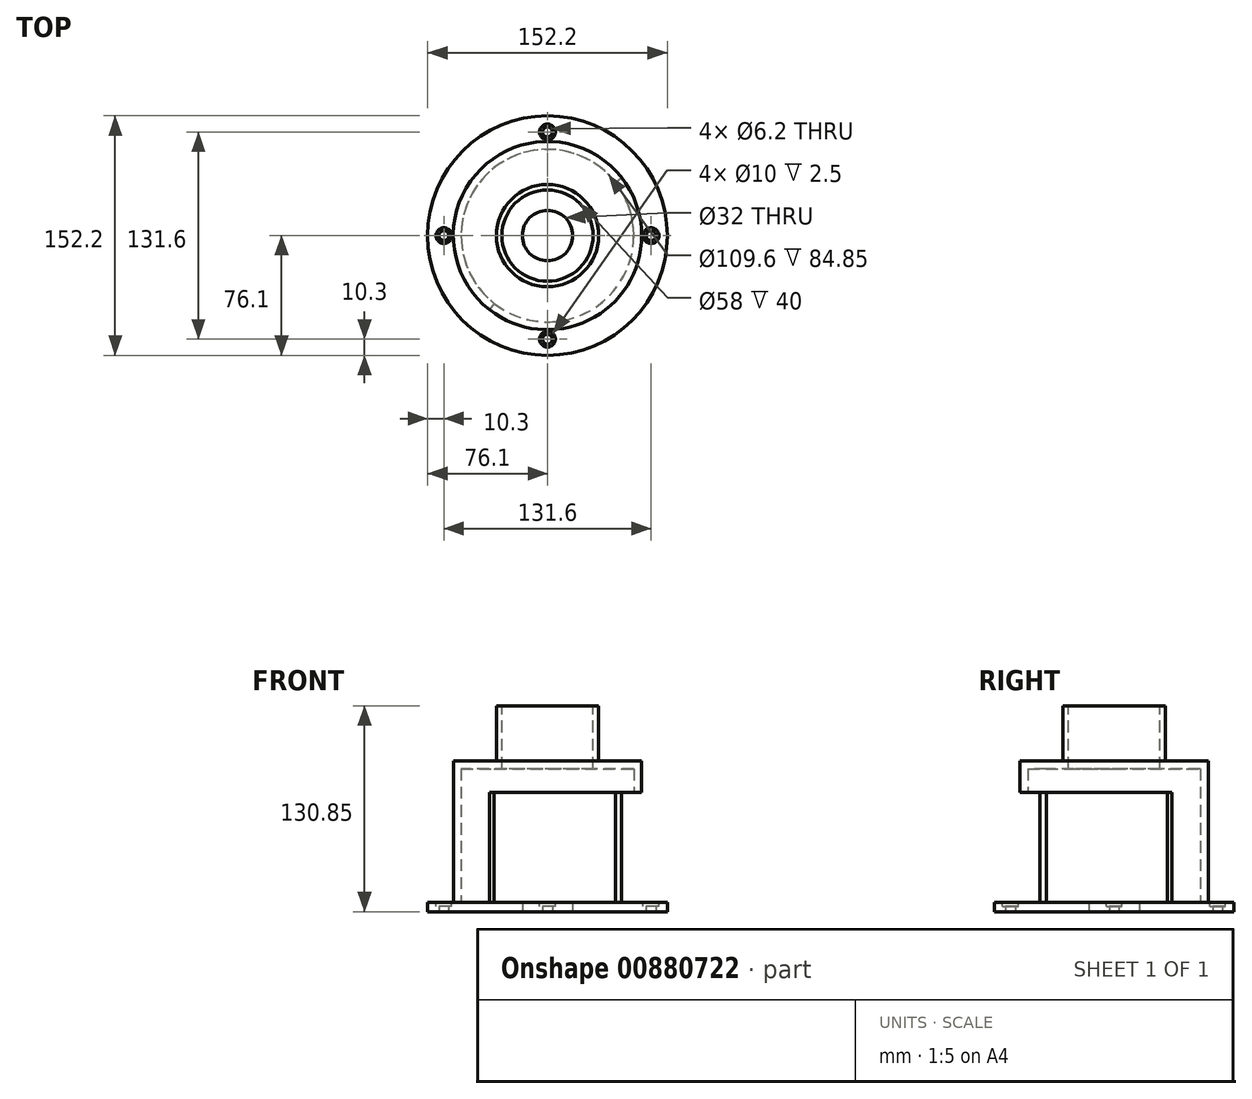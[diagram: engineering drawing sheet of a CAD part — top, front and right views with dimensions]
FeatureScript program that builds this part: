
annotation { "Feature Type Name" : "Feature", "Feature Type Description" : "" }
export const myFeature = defineFeature(function(context is Context, id is Id, definition is map)
    precondition{}
    {
        {
            var Q0;
            Q0=qCreatedBy(makeId("Top.planeOp"),FACE);
            var sketch = newSketch(context, id + "F0", { "sketchPlane" : qUnion([Q0])});
            skCircle(sketch, "E0", {"center": v(0, 0) * mm, "radius": 76.1 * mm});
            skSolve(sketch);
        }
        {
            var Q0;
            Q0 = qSketchRegion(id + "F0", true);
            extrude(context, id + "F1", {"entities" : qUnion([Q0]), "depth" : 6 * mm, "offsetDistance" : 25 * mm});
        }
        {
            var Q0;
            Q0=qCreatedBy(makeId("Top.planeOp"),FACE);
            var sketch = newSketch(context, id + "F2", { "sketchPlane" : qUnion([Q0])});
            skCircle(sketch, "E1", {"center": v(0, 65.8) * mm, "radius": 3.1 * mm});
            skCircle(sketch, "E2", {"center": v(65.8, 0) * mm, "radius": 3.1 * mm});
            skCircle(sketch, "E3", {"center": v(0, -65.8) * mm, "radius": 3.1 * mm});
            skCircle(sketch, "E4", {"center": v(-65.8, 0) * mm, "radius": 3.1 * mm});
            skCircle(sketch, "E5", {"center": v(0, 0) * mm, "radius": 16 * mm});
            skSolve(sketch);
        }
        {
            var Q0;
            Q0 = qSketchRegion(id + "F2", true);
            var Q1;
            Q1=makeQuery(id+"F1.opExtrude","CAP_FACE",FACE,{"disambiguationData":[OSD([sQuery(id+"F0.wireOp",EDGE,"E0")])],"isStart":false});
            extrude(context, id + "F3", {"entities" : qUnion([Q0]), "operationType" : NewBodyOperationType.REMOVE, "endBound" : BoundingType.UP_TO_SURFACE, "depth" : 25 * mm, "endBoundEntityFace" : qUnion([Q1]), "offsetDistance" : 25 * mm});
        }
        {
            var Q0;
            Q0=makeQuery(id+"F1.opExtrude","CAP_FACE",FACE,{"disambiguationData":[OSD([sQuery(id+"F0.wireOp",EDGE,"E0")])],"isStart":false});
            cPlane(context, id + "F4", {"entities" : qUnion([Q0]), "cplaneType" : CPlaneType.OFFSET, "offset" : 0 * mm, "width" : 150 * mm, "height" : 150 * mm});
        }
        {
            var Q0;
            Q0=qCreatedBy(id+"F4.planeOp",FACE);
            var sketch = newSketch(context, id + "F5", { "sketchPlane" : qUnion([Q0])});
            skCircle(sketch, "E6", {"center": v(-0.09, 0) * mm, "radius": 59.89 * mm, "construction": true});
            skCircle(sketch, "E7", {"center": v(0, 0) * mm, "radius": 54.8 * mm, "construction": true});
            skCircle(sketch, "E8.0", {"center": v(65.8, 0) * mm, "radius": 3.1 * mm, "construction": true});
            skLineSegment(sketch, "E9", {"start": v(-0.09, 0) * mm, "end": v(-36.96, -47.2) * mm, "construction": true});
            skLineSegment(sketch, "E10", {"start": v(0, 0) * mm, "end": v(47.14, 36.83) * mm, "construction": true});
            skArc(sketch, "E11", {"start": v(47.14, 36.83) * mm, "mid": v(-42.27, 42.32) * mm, "end": v(-36.88, -47.1) * mm});
            skArc(sketch, "E12", {"start": v(43.18, 33.74) * mm, "mid": v(-38.72, 38.77) * mm, "end": v(-33.8, -43.14) * mm});
            skLineSegment(sketch, "E13", {"start": v(-33.8, -43.14) * mm, "end": v(-36.88, -47.1) * mm});
            skLineSegment(sketch, "E14", {"start": v(43.18, 33.74) * mm, "end": v(47.14, 36.83) * mm});
            skCircle(sketch, "E15", {"center": v(0, 0) * mm, "radius": 12.7 * mm, "construction": true});
            skLineSegment(sketch, "E16", {"start": v(47.14, 36.83) * mm, "end": v(-36.88, -47.1) * mm, "construction": true});
            skSolve(sketch);
        }
        {
            var Q0;
            Q0 = qSketchRegion(id + "F5", true);
            extrude(context, id + "F6", {"entities" : qUnion([Q0]), "operationType" : NewBodyOperationType.ADD, "depth" : 69.85 * mm, "offsetDistance" : 25 * mm});
        }
        {
            var Q0;
            Q0=makeQuery(id+"F6.opExtrude","CAP_FACE",FACE,{"disambiguationData":[OSD([sQuery(id+"F5.wireOp",EDGE,"E11"),sQuery(id+"F5.wireOp",EDGE,"E12"),sQuery(id+"F5.wireOp",EDGE,"E13"),sQuery(id+"F5.wireOp",EDGE,"E14")])],"isStart":false});
            cPlane(context, id + "F7", {"entities" : qUnion([Q0]), "cplaneType" : CPlaneType.OFFSET, "offset" : 0 * mm, "width" : 150 * mm, "height" : 150 * mm});
        }
        {
            var Q0;
            Q0=qCreatedBy(id+"F7.planeOp",FACE);
            var sketch = newSketch(context, id + "F8", { "sketchPlane" : qUnion([Q0])});
            skCircle(sketch, "E17", {"center": v(0, 0) * mm, "radius": 59.82 * mm});
            skCircle(sketch, "E18", {"center": v(0, 0) * mm, "radius": 54.8 * mm});
            skArc(sketch, "E19.0", {"start": v(43.18, 33.74) * mm, "mid": v(-38.72, 38.77) * mm, "end": v(-33.8, -43.14) * mm, "construction": true});
            skArc(sketch, "E19.1", {"start": v(47.14, 36.83) * mm, "mid": v(-42.27, 42.32) * mm, "end": v(-36.88, -47.1) * mm, "construction": true});
            skSolve(sketch);
        }
        {
            var Q0;
            Q0 = qSketchRegion(id + "F8", true);
            extrude(context, id + "F9", {"entities" : qUnion([Q0]), "operationType" : NewBodyOperationType.ADD, "depth" : 15 * mm, "offsetDistance" : 25 * mm});
        }
        {
            var Q0;
            Q0=makeQuery(id+"F9.opExtrude","CAP_FACE",FACE,{"disambiguationData":[OSD([sQuery(id+"F8.wireOp",EDGE,"E17"),sQuery(id+"F8.wireOp",EDGE,"E18")])],"isStart":false});
            cPlane(context, id + "F10", {"entities" : qUnion([Q0]), "cplaneType" : CPlaneType.OFFSET, "offset" : 0 * mm, "width" : 150 * mm, "height" : 150 * mm});
        }
        {
            var Q0;
            Q0=qCreatedBy(id+"F10.planeOp",FACE);
            var sketch = newSketch(context, id + "F11", { "sketchPlane" : qUnion([Q0])});
            skCircle(sketch, "E20.0", {"center": v(0, 0) * mm, "radius": 59.82 * mm});
            skSolve(sketch);
        }
        {
            var Q0;
            Q0 = qSketchRegion(id + "F11", true);
            extrude(context, id + "F12", {"entities" : qUnion([Q0]), "operationType" : NewBodyOperationType.ADD, "depth" : 5 * mm, "offsetDistance" : 25 * mm});
        }
        {
            var Q0;
            Q0=makeQuery(id+"F12.opExtrude","CAP_FACE",FACE,{"disambiguationData":[OSD([sQuery(id+"F11.wireOp",EDGE,"E20.0")])],"isStart":false});
            cPlane(context, id + "F13", {"entities" : qUnion([Q0]), "cplaneType" : CPlaneType.OFFSET, "offset" : 0 * mm, "width" : 150 * mm, "height" : 150 * mm});
        }
        {
            var Q0;
            Q0=qCreatedBy(id+"F13.planeOp",FACE);
            var sketch = newSketch(context, id + "F14", { "sketchPlane" : qUnion([Q0])});
            skCircle(sketch, "E21", {"center": v(0, 0) * mm, "radius": 32.5 * mm});
            skSolve(sketch);
        }
        {
            var Q0;
            Q0 = qSketchRegion(id + "F14", true);
            extrude(context, id + "F15", {"entities" : qUnion([Q0]), "operationType" : NewBodyOperationType.ADD, "depth" : 35 * mm, "offsetDistance" : 25 * mm});
        }
        {
            var Q0;
            Q0=makeQuery(id+"F15.opExtrude","CAP_FACE",FACE,{"disambiguationData":[OSD([sQuery(id+"F14.wireOp",EDGE,"E21")])],"isStart":false});
            cPlane(context, id + "F16", {"entities" : qUnion([Q0]), "cplaneType" : CPlaneType.OFFSET, "offset" : 0 * mm, "width" : 150 * mm, "height" : 150 * mm});
        }
        {
            var Q0;
            Q0=qCreatedBy(id+"F16.planeOp",FACE);
            var sketch = newSketch(context, id + "F17", { "sketchPlane" : qUnion([Q0])});
            skCircle(sketch, "E22", {"center": v(0, 0) * mm, "radius": 29 * mm});
            skSolve(sketch);
        }
        {
            var Q0;
            Q0 = qSketchRegion(id + "F17", true);
            var Q1;
            Q1=makeQuery(id+"F12.opExtrude","CAP_FACE",FACE,{"disambiguationData":[OSD([sQuery(id+"F11.wireOp",EDGE,"E20.0")])],"isStart":true});
            extrude(context, id + "F18", {"entities" : qUnion([Q0]), "operationType" : NewBodyOperationType.REMOVE, "endBound" : BoundingType.UP_TO_SURFACE, "oppositeDirection" : true, "depth" : 25 * mm, "endBoundEntityFace" : qUnion([Q1]), "offsetDistance" : 25 * mm});
        }
        {
            var Q0;
            Q0=qCreatedBy(id+"F4.planeOp",FACE);
            var sketch = newSketch(context, id + "F19", { "sketchPlane" : qUnion([Q0])});
            skCircle(sketch, "E23.0", {"center": v(-65.8, 0) * mm, "radius": 3.1 * mm, "construction": true});
            skCircle(sketch, "E24.0", {"center": v(0, 65.8) * mm, "radius": 3.1 * mm, "construction": true});
            skCircle(sketch, "E25.0", {"center": v(0, -65.8) * mm, "radius": 3.1 * mm, "construction": true});
            skCircle(sketch, "E26.0", {"center": v(65.8, 0) * mm, "radius": 3.1 * mm, "construction": true});
            skCircle(sketch, "E27", {"center": v(-65.8, 0) * mm, "radius": 5 * mm});
            skCircle(sketch, "E28", {"center": v(0, 65.8) * mm, "radius": 5 * mm});
            skCircle(sketch, "E29", {"center": v(65.8, 0) * mm, "radius": 5 * mm});
            skCircle(sketch, "E30", {"center": v(0, -65.8) * mm, "radius": 5 * mm});
            skSolve(sketch);
        }
        {
            var Q0;
            Q0 = qSketchRegion(id + "F19", true);
            extrude(context, id + "F20", {"entities" : qUnion([Q0]), "operationType" : NewBodyOperationType.REMOVE, "oppositeDirection" : true, "depth" : 2.5 * mm, "offsetDistance" : 25 * mm});
        }
    });
